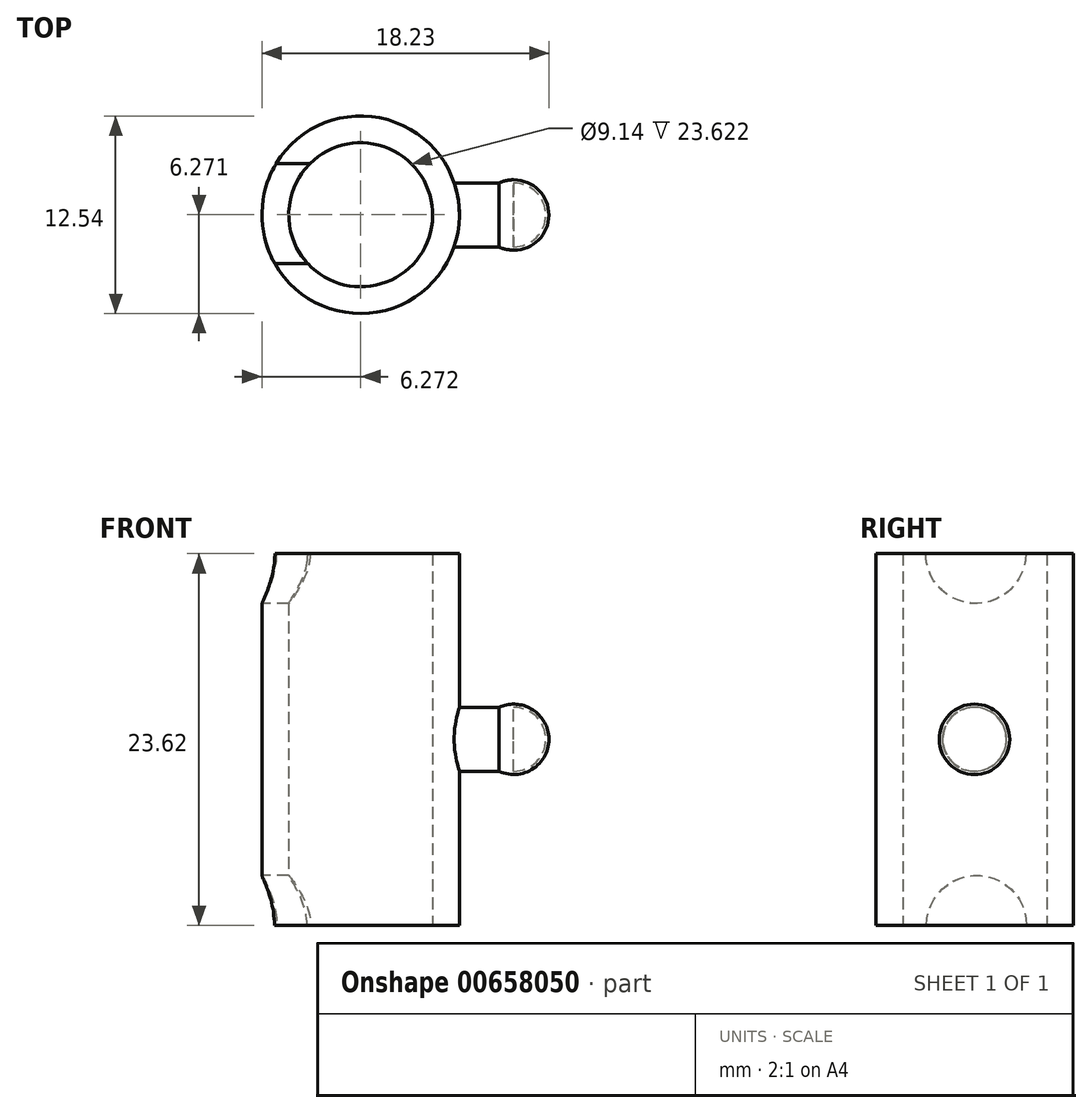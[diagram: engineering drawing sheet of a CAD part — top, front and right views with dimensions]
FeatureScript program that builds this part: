
annotation { "Feature Type Name" : "Feature", "Feature Type Description" : "" }
export const myFeature = defineFeature(function(context is Context, id is Id, definition is map)
    precondition{}
    {
        {
            var Q0;
            Q0=qCreatedBy(makeId("Top.planeOp"),FACE);
            var sketch = newSketch(context, id + "F0", { "sketchPlane" : qUnion([Q0])});
            skCircle(sketch, "E0", {"center": v(-43.27, 13.76) * mm, "radius": 4.57 * mm});
            skCircle(sketch, "E1.0", {"center": v(-43.27, 13.76) * mm, "radius": 6.27 * mm});
            skSolve(sketch);
        }
        {
            var Q0;
            Q0=qSketchRegion(id+"F0",true);
            extrude(context, id + "F1", {"entities" : qUnion([Q0]), "depth" : 23.62 * mm, "offsetDistance" : 25.4 * mm});
        }
        {
            var Q0;
            Q0=qCreatedBy(makeId("Right.planeOp"),FACE);
            cPlane(context, id + "F2", {"entities" : qUnion([Q0]), "cplaneType" : CPlaneType.OFFSET, "offset" : 35.53 * mm, "oppositeDirection" : true, "width" : 152.4 * mm, "height" : 152.4 * mm});
        }
        {
            var Q0;
            Q0=qCreatedBy(id+"F2.planeOp",FACE);
            var sketch = newSketch(context, id + "F3", { "sketchPlane" : qUnion([Q0])});
            skCircle(sketch, "E2", {"center": v(13.75, 11.82) * mm, "radius": 2.03 * mm});
            skPoint(sketch, "E3.start.orphan", {"position": v(5.99, 0) * mm});
            skPoint(sketch, "E4.end.orphan", {"position": v(21.4, 0) * mm});
            skSolve(sketch);
        }
        {
            var Q0;
            Q0=makeQuery(id+"F3.imprint","IMPRINT",FACE,{"disambiguationData":[TD([[makeQuery(id+"F3.imprint","IMPRINT",EDGE,{"derivedFrom":sQuery(id+"F3.wireOp",EDGE,"E2")}),1.0]])]});
            extrude(context, id + "F4", {"entities" : qUnion([Q0]), "operationType" : NewBodyOperationType.ADD, "endBound" : BoundingType.SYMMETRIC, "depth" : 3.96 * mm, "offsetDistance" : 25.4 * mm});
        }
        {
            var Q0;
            Q0=makeQuery(id+"F4.opExtrude","CAP_FACE",FACE,{"disambiguationData":[OSD([sQuery(id+"F3.wireOp",EDGE,"E2")])],"isStart":false});
            var sketch = newSketch(context, id + "F5", { "sketchPlane" : qUnion([Q0])});
            skLineSegment(sketch, "E5", {"start": v(13.75, 11.82) * mm, "end": v(11.51, 11.82) * mm});
            skLineSegment(sketch, "E6", {"start": v(13.75, 11.82) * mm, "end": v(15.98, 11.82) * mm});
            skArc(sketch, "E7.0", {"start": v(15.98, 11.82) * mm, "mid": v(13.75, 14.06) * mm, "end": v(11.51, 11.82) * mm});
            skSolve(sketch);
        }
        {
            var Q0;
            {var subQ0=sQuery(id+"F5.wireOp",EDGE,"E7.0");Q0=makeQuery(id+"F5.imprint","IMPRINT",FACE,{"disambiguationData":[TD([[makeQuery(id+"F5.imprint","IMPRINT",EDGE,{"derivedFrom":subQ0}),1.0]])]});}
            var Q1;
            Q1=sQuery(id+"F5.wireOp",EDGE,"E5");
            revolve(context, id + "F6", {"operationType" : NewBodyOperationType.ADD, "entities" : qUnion([Q0]), "axis" : qUnion([Q1]), "revolveType" : RevolveType.FULL});
        }
        {
            var Q0;
            Q0=qCreatedBy(makeId("Right.planeOp"),FACE);
            cPlane(context, id + "F7", {"entities" : qUnion([Q0]), "cplaneType" : CPlaneType.OFFSET, "offset" : 51.04 * mm, "oppositeDirection" : true, "width" : 152.4 * mm, "height" : 152.4 * mm});
        }
        {
            var Q0;
            Q0=qCreatedBy(id+"F7.planeOp",FACE);
            var sketch = newSketch(context, id + "F8", { "sketchPlane" : qUnion([Q0])});
            skCircle(sketch, "E8", {"center": v(13.83, 23.62) * mm, "radius": 3.18 * mm});
            skCircle(sketch, "E9", {"center": v(13.88, 0) * mm, "radius": 3.18 * mm});
            skPoint(sketch, "E10.orphan", {"position": v(21.65, 0) * mm});
            skPoint(sketch, "E11.orphan", {"position": v(6.11, 0) * mm});
            skSolve(sketch);
        }
        {
            var Q0;
            Q0=makeQuery(id+"F8.imprint","IMPRINT",FACE,{"disambiguationData":[TD([[makeQuery(id+"F8.imprint","IMPRINT",EDGE,{"derivedFrom":sQuery(id+"F8.wireOp",EDGE,"E8")}),1.0]])]});
            var Q1;
            Q1=makeQuery(id+"F8.imprint","IMPRINT",FACE,{"disambiguationData":[TD([[makeQuery(id+"F8.imprint","IMPRINT",EDGE,{"derivedFrom":sQuery(id+"F8.wireOp",EDGE,"E9")}),1.0]])]});
            extrude(context, id + "F9", {"entities" : qUnion([Q0, Q1]), "operationType" : NewBodyOperationType.REMOVE, "depth" : 8.64 * mm, "offsetDistance" : 25.4 * mm});
        }
    });
